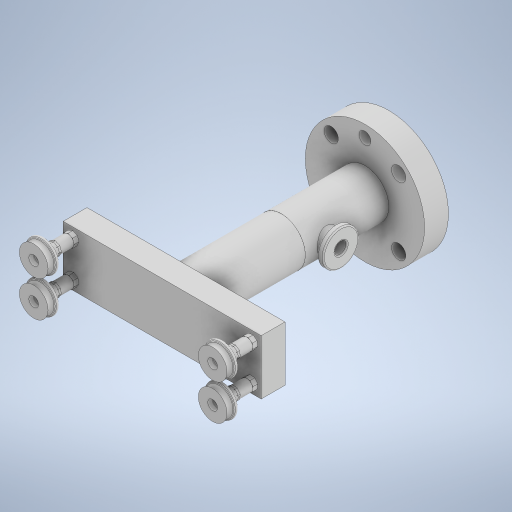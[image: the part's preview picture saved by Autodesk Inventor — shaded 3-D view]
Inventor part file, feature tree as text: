
AUTODESK INVENTOR PART (.ipt)
format: ipt  version: 2024 (Build 280153000, 153)  size: 1,016,320 bytes
history: native  units: mm
features: other x30, sketch x2
ambient origin geometry x8: Origin, YZ Plane, XZ Plane, XY Plane, X Axis, Y Axis, Z Axis, Center Point
bodies: Body1 (feature_tree), Body2 (feature_tree), Body3 (feature_tree), Body4 (feature_tree), Body5 (feature_tree), Body6 (feature_tree), Body7 (feature_tree), Body8 (feature_tree), Body9 (feature_tree), Body10 (feature_tree), Body11 (feature_tree), Body12 (feature_tree), Body13 (feature_tree), Body14 (feature_tree)
feature tree (32):
  other  "ENSAMBLAJE_VENTOSA_2.iam"
  other  "ACOPLE.ipt:1"
  other  "TORNILLO_B.ipt:4"
  other  "TUBO_METALICO_B.ipt:4"
  other  "VENTOSA_B.ipt:4"
  other  "UNION_B.ipt:1"
  other  "TORNILLO_B_MIR.ipt:1"
  other  "TUBO_METALICO_B_MIR.ipt:1"
  other  "VENTOSA_B_MIR.ipt:1"
  other  "TORNILLO_B_MIR1.ipt:1"
  other  "TUBO_METALICO_B_MIR1.ipt:1"
  other  "VENTOSA_B_MIR1.ipt:1"
  other  "TORNILLO_B_MIR_MIR.ipt:1"
  other  "TUBO_METALICO_B_MIR_MIR.ipt:1"
  other  "VENTOSA_B_MIR_MIR.ipt:1"
  other  "Sólido1"
  other  "Desplazar cuerpo1"
  sketch  "Boceto 1"  dims[d0=10.0mm]
  sketch  "Boceto 2"  dims[d1=-0.101mm d2=0.065mm d3=0.0mm]
  other  "Sólido2"
  other  "Sólido3"
  other  "Sólido4"
  other  "Sólido5"
  other  "Sólido6"
  other  "Sólido7"
  other  "Sólido8"
  other  "Sólido9"
  other  "Sólido10"
  other  "Sólido11"
  other  "Sólido12"
  other  "Sólido13"
  other  "Sólido14"
